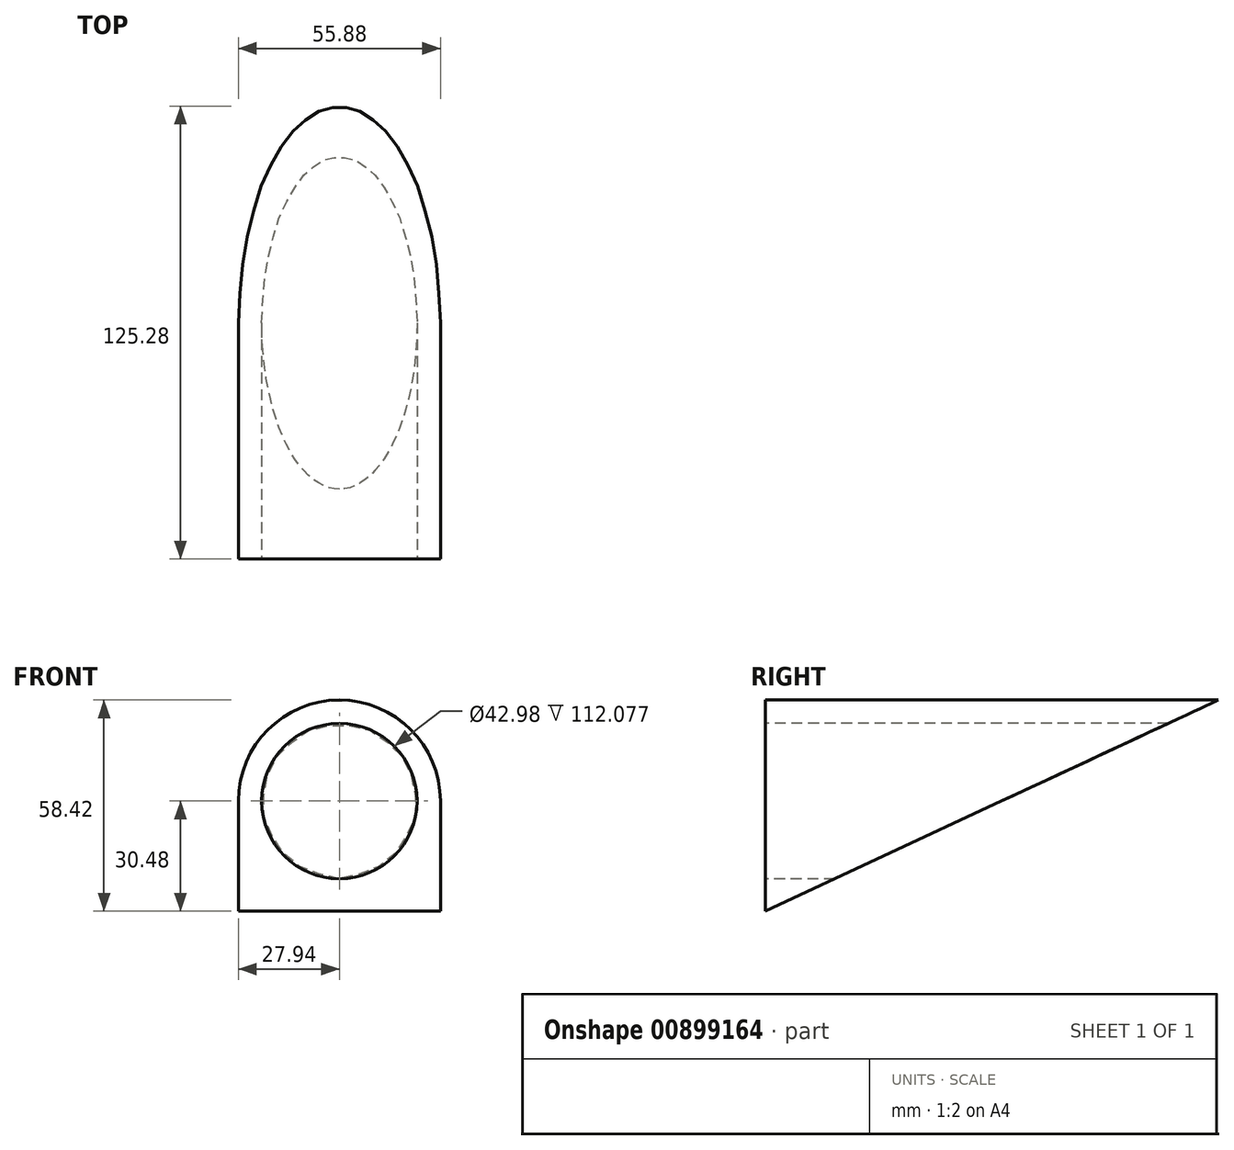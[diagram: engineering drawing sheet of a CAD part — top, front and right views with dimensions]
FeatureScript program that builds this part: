
annotation { "Feature Type Name" : "Feature", "Feature Type Description" : "" }
export const myFeature = defineFeature(function(context is Context, id is Id, definition is map)
    precondition{}
    {
        {
            var Q0;
            Q0=qCreatedBy(makeId("Front.planeOp"),FACE);
            var sketch = newSketch(context, id + "F0", { "sketchPlane" : qUnion([Q0])});
            skLineSegment(sketch, "E0.bottom", {"start": v(27.94, 15.24) * mm, "end": v(-27.94, 15.24) * mm});
            skLineSegment(sketch, "E0.top", {"start": v(27.94, -15.24) * mm, "end": v(-27.94, -15.24) * mm});
            skLineSegment(sketch, "E0.left", {"start": v(27.94, 15.24) * mm, "end": v(27.94, -15.24) * mm});
            skLineSegment(sketch, "E0.right", {"start": v(-27.94, 15.24) * mm, "end": v(-27.94, -15.24) * mm});
            skPoint(sketch, "E0.middle", {"position": v(0, 0) * mm});
            skArc(sketch, "E1", {"start": v(-27.94, 15.24) * mm, "mid": v(0, 43.18) * mm, "end": v(27.94, 15.24) * mm});
            skSolve(sketch);
        }
        {
            var Q0;
            Q0=makeQuery(id+"F0.imprint","IMPRINT",FACE,{"disambiguationData":[TD([[makeQuery(id+"F0.imprint","IMPRINT",EDGE,{"derivedFrom":sQuery(id+"F0.wireOp",EDGE,"E0.bottom")}),-1.0]])]});
            var Q1;
            Q1=makeQuery(id+"F0.imprint","IMPRINT",FACE,{"disambiguationData":[TD([[makeQuery(id+"F0.imprint","IMPRINT",EDGE,{"derivedFrom":sQuery(id+"F0.wireOp",EDGE,"E0.bottom")}),1.0]])]});
            extrude(context, id + "F1", {"entities" : qUnion([Q0, Q1]), "oppositeDirection" : true, "depth" : 127 * mm, "offsetDistance" : 25.4 * mm});
        }
        {
            var Q0;
            Q0=makeQuery(id+"F1.opExtrude","CAP_FACE",FACE,{"disambiguationData":[OSD([sQuery(id+"F0.wireOp",EDGE,"E0.top"),sQuery(id+"F0.wireOp",EDGE,"E0.left"),sQuery(id+"F0.wireOp",EDGE,"E0.right"),sQuery(id+"F0.wireOp",EDGE,"E1")])],"isStart":true});
            var sketch = newSketch(context, id + "F2", { "sketchPlane" : qUnion([Q0])});
            skCircle(sketch, "E2", {"center": v(0, 15.24) * mm, "radius": 21.49 * mm});
            skSolve(sketch);
        }
        {
            var Q0;
            Q0=makeQuery(id+"F2.imprint","IMPRINT",FACE,{"disambiguationData":[TD([[makeQuery(id+"F2.imprint","IMPRINT",EDGE,{"derivedFrom":sQuery(id+"F2.wireOp",EDGE,"E2")}),1.0]])]});
            extrude(context, id + "F3", {"entities" : qUnion([Q0]), "operationType" : NewBodyOperationType.REMOVE, "endBound" : BoundingType.THROUGH_ALL, "oppositeDirection" : true, "depth" : 25.4 * mm, "offsetDistance" : 25.4 * mm});
        }
        {
            var Q0;
            Q0=makeQuery(id+"F1.opExtrude","SWEPT_FACE",FACE,{"disambiguationData":[OSD([sQuery(id+"F0.wireOp",EDGE,"E0.left")])]});
            var sketch = newSketch(context, id + "F4", { "sketchPlane" : qUnion([Q0])});
            skLineSegment(sketch, "E3", {"start": v(0, -15.24) * mm, "end": v(267.64, 109.56) * mm});
            skLineSegment(sketch, "E4", {"start": v(267.64, 109.56) * mm, "end": v(267.64, -15.24) * mm});
            skLineSegment(sketch, "E5", {"start": v(267.64, -15.24) * mm, "end": v(0, -15.24) * mm});
            skSolve(sketch);
        }
        {
            var Q0;
            Q0 = qSketchRegion(id + "F4", true);
            extrude(context, id + "F5", {"entities" : qUnion([Q0]), "operationType" : NewBodyOperationType.REMOVE, "endBound" : BoundingType.THROUGH_ALL, "oppositeDirection" : true, "depth" : 25.4 * mm, "offsetDistance" : 25.4 * mm});
        }
    });
